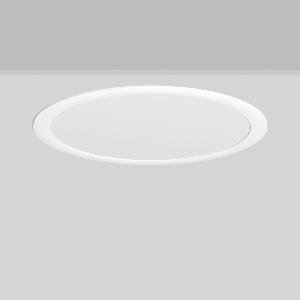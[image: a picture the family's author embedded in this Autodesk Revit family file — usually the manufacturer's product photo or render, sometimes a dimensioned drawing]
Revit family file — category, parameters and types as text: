
# Revit family: toledo_flat_round_e_672385_002_1_07_27f4
name_source: partatom
category: Lighting Fixtures
units: mm (PartAtom-declared; Revit-internal decimal feet)

## family parameters
Cut with Voids When Loaded = No
Host = Face
Light Source = No
Part Type = Normal
Room Calculation Point = No
Round Connector Dimension = Use Diameter
Shared = No

## types (1)
- TOLEDO FLAT round E (1 x LED Modul 840, 3600 lm, 4000)
    Apparent Load = 30 VA
    CIE Flux Codes = 48 79 96 100 100
    Color Rendering = 80
    Color Temperature = 4000
    Default Elevation = 1800 mm
    Description = Series: TOLEDO FLAT round
Ultra thin recessed downlight. For escape route illumination. Housing: die-cast aluminium, powder-coated. Ceiling installation with spring system. Including separate LED converter with connecting cable 250 mm. Self-contained system with automatic self-test and feedback via DALI bus, only to RZB DALI monitoring system. External driver with simple plug-in locking system. 
Colour: white
Diameter: 495 mm
Height: 6 mm
Cut-out diameter: 470 mm
Recess height: 70 mm
Luminaire: recess height: 60-80 mm
Weight: 3.38 kg
Operating mode: maintained power mode
Duration time: 8 h
Lamp: LED
Socket: without socket
Colour temperature: 4000K
Colour rendering index (CRI): 80
System power: 30 W
Rated luminous flux: 3600 lm
Luminous flux, emergency: 170 lm
System power, emergency: -
Control gear: Regulated power supply
Protection class: I
Type of protection: IP 54
    Height = 0 mm  [stored 0 ft]
    Lamp = 1 x LED Modul 840
    Lamp Light Flux = 3600 lm
    Lamp count = 1
    Length = 495 mm
    Lifetime = 50000 h
    Luminous efficacy = 120 lm/W
    Manufacturer = RZB
    ModVariant = No
    Model = 672385.002.1.07
    Mounting Place = Ceiling
    Mounting Type = Recessed
    Number of Poles = 1
    OnlyDefault = Yes
    Power Factor = 1
    Product Name = TOLEDO FLAT round E
    Product group = Recessed downlights
    ProductGroupID = 402
    Protection Class = Protection class I
    Protection Degree = IP 40
    RLX_Detail_Level = 1
    RLX_Emergency_Light_Flux = 170 lm
    RLX_Emergency_Type = 3
    RLX_Emergency_Type_DB = Yes
    RlxData = <blob elided: 35193 chars, md5=40e37c70>
    Socket = socket
    Standby Power = 0 W
    System Light Flux = 3600 lm
    System Power = 30 W
    Type Comments = Product without accessories
    Type Image = 901585.002.jpg
    URL = http://relux.com
    VarID = ---
    Voltage = 230 V
    Voltage Range = 220-240 V
    Weight = 0.00 kg
    Width = 0 mm  [stored 0 ft]

note: [stored X ft] marks values corroborated as IEEE doubles in the binary element streams (Revit-internal decimal feet)

## geometry (parser evidence)
native form markers: Blend x4, Sweep x12
no freeform markers — native parametric forms only
